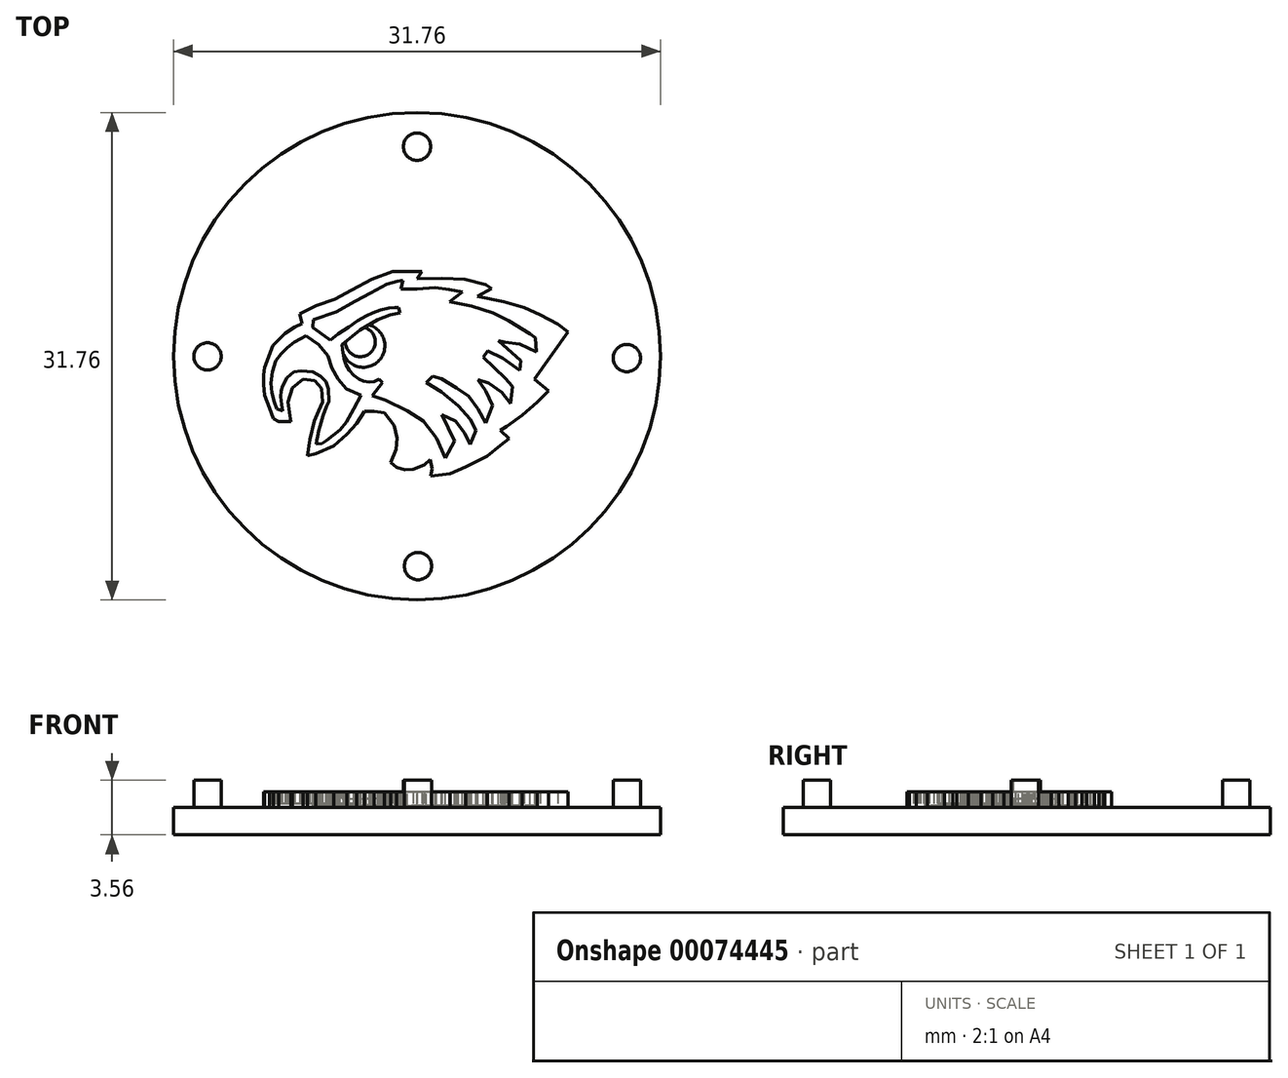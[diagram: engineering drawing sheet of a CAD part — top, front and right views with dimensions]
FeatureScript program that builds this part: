
annotation { "Feature Type Name" : "Feature", "Feature Type Description" : "" }
export const myFeature = defineFeature(function(context is Context, id is Id, definition is map)
    precondition{}
    {
        {
            var Q0;
            Q0=qCreatedBy(makeId("Top.planeOp"),FACE);
            var sketch = newSketch(context, id + "F0", { "sketchPlane" : qUnion([Q0])});
            skCircle(sketch, "E0", {"center": v(0, 0) * mm, "radius": 15.88 * mm});
            skSolve(sketch);
        }
        {
            var Q0;
            Q0=qSketchRegion(id+"F0",true);
            extrude(context, id + "F1", {"entities" : qUnion([Q0]), "oppositeDirection" : true, "depth" : 1.78 * mm});
        }
        {
            var Q0;
            Q0=makeQuery(id+"F1.opExtrude","CAP_FACE",FACE,{"disambiguationData":[OSD([sQuery(id+"F0.wireOp",EDGE,"E0")])],"isStart":true});
            var sketch = newSketch(context, id + "F2", { "sketchPlane" : qUnion([Q0])});
            skCircle(sketch, "E1", {"center": v(0, 0) * mm, "radius": 12.7 * mm});
            skSolve(sketch);
        }
        {
            var Q0;
            Q0=makeQuery(id+"F2.imprint","IMPRINT",FACE,{"disambiguationData":[TD([[makeQuery(id+"F2.imprint","IMPRINT",EDGE,{"derivedFrom":sQuery(id+"F2.wireOp",EDGE,"E1")}),-1.0]])]});
            var sketch = newSketch(context, id + "F3", { "sketchPlane" : qUnion([Q0])});
            skCircle(sketch, "E2", {"center": v(0, 13.65) * mm, "radius": 0.89 * mm});
            skCircle(sketch, "E3", {"center": v(-13.66, -0.02) * mm, "radius": 0.89 * mm});
            skCircle(sketch, "E4", {"center": v(0.06, -13.68) * mm, "radius": 0.89 * mm});
            skCircle(sketch, "E5", {"center": v(13.67, -0.12) * mm, "radius": 0.89 * mm});
            skSolve(sketch);
        }
        {
            var Q0;
            Q0=qSketchRegion(id+"F3",true);
            extrude(context, id + "F4", {"entities" : qUnion([Q0]), "operationType" : NewBodyOperationType.ADD, "depth" : 1.78 * mm});
        }
        {
            var Q0;
            Q0=makeQuery(id+"F2.imprint","IMPRINT",FACE,{"disambiguationData":[TD([[makeQuery(id+"F2.imprint","IMPRINT",EDGE,{"derivedFrom":sQuery(id+"F2.wireOp",EDGE,"E1")}),-1.0]])]});
            var sketch = newSketch(context, id + "F5", { "sketchPlane" : qUnion([Q0])});
            skLineSegment(sketch, "E6", {"start": v(-9.93, -2.55) * mm, "end": v(-10, -1.84) * mm});
            skLineSegment(sketch, "E7", {"start": v(-10, -1.22) * mm, "end": v(-9.93, -0.75) * mm});
            skLineSegment(sketch, "E8", {"start": v(-9.93, -0.75) * mm, "end": v(-9.42, 0.69) * mm});
            skLineSegment(sketch, "E9", {"start": v(-9.42, 0.69) * mm, "end": v(-8.6, 1.5) * mm});
            skLineSegment(sketch, "E10", {"start": v(-8.6, 1.5) * mm, "end": v(-7.97, 1.88) * mm});
            skLineSegment(sketch, "E11", {"start": v(-7.97, 1.88) * mm, "end": v(-7.5, 2.11) * mm});
            skLineSegment(sketch, "E12", {"start": v(-7.5, 2.11) * mm, "end": v(-7.66, 2.74) * mm});
            skLineSegment(sketch, "E13", {"start": v(-7.66, 2.74) * mm, "end": v(-6.58, 3.29) * mm});
            skLineSegment(sketch, "E14", {"start": v(-6.58, 3.29) * mm, "end": v(-5.36, 3.7) * mm});
            skLineSegment(sketch, "E15", {"start": v(-5.36, 3.7) * mm, "end": v(-4.25, 4.3) * mm});
            skLineSegment(sketch, "E16", {"start": v(-4.25, 4.3) * mm, "end": v(-2.97, 5.01) * mm});
            skLineSegment(sketch, "E17", {"start": v(-2.97, 5.01) * mm, "end": v(-1.58, 5.52) * mm});
            skLineSegment(sketch, "E18", {"start": v(-1.58, 5.52) * mm, "end": v(-1.4, 5.52) * mm});
            skLineSegment(sketch, "E19", {"start": v(-1.4, 5.52) * mm, "end": v(0, 5.52) * mm});
            skLineSegment(sketch, "E20", {"start": v(-0.55, 5.52) * mm, "end": v(0, 5.52) * mm});
            skLineSegment(sketch, "E21", {"start": v(-0.55, 5.52) * mm, "end": v(0.33, 5.52) * mm});
            skLineSegment(sketch, "E22", {"start": v(0.33, 5.52) * mm, "end": v(0, 5.04) * mm});
            skLineSegment(sketch, "E23", {"start": v(0, 5.04) * mm, "end": v(1.62, 5.08) * mm});
            skLineSegment(sketch, "E24", {"start": v(1.62, 5.08) * mm, "end": v(3.1, 5.01) * mm});
            skLineSegment(sketch, "E25", {"start": v(3.1, 5.01) * mm, "end": v(4.46, 4.67) * mm});
            skLineSegment(sketch, "E26", {"start": v(4.46, 4.67) * mm, "end": v(4.87, 4.4) * mm});
            skLineSegment(sketch, "E27", {"start": v(4.87, 4.4) * mm, "end": v(3.92, 3.9) * mm});
            skLineSegment(sketch, "E28", {"start": v(3.92, 3.9) * mm, "end": v(5.64, 3.56) * mm});
            skLineSegment(sketch, "E29", {"start": v(5.64, 3.56) * mm, "end": v(7, 3.15) * mm});
            skLineSegment(sketch, "E30", {"start": v(7, 3.15) * mm, "end": v(8.04, 2.68) * mm});
            skLineSegment(sketch, "E31", {"start": v(8.04, 2.68) * mm, "end": v(9.19, 2.07) * mm});
            skLineSegment(sketch, "E32", {"start": v(9.19, 2.07) * mm, "end": v(9.83, 1.57) * mm});
            skLineSegment(sketch, "E33", {"start": v(9.83, 1.57) * mm, "end": v(7.63, -1.5) * mm});
            skLineSegment(sketch, "E34", {"start": v(7.63, -1.5) * mm, "end": v(8.58, -2.25) * mm});
            skLineSegment(sketch, "E35", {"start": v(8.58, -2.25) * mm, "end": v(7.84, -3) * mm});
            skLineSegment(sketch, "E36", {"start": v(7.84, -3) * mm, "end": v(6.86, -3.83) * mm});
            skLineSegment(sketch, "E37", {"start": v(6.86, -3.83) * mm, "end": v(5.84, -4.58) * mm});
            skLineSegment(sketch, "E38", {"start": v(5.84, -4.58) * mm, "end": v(5.44, -4.85) * mm});
            skLineSegment(sketch, "E39", {"start": v(5.44, -4.85) * mm, "end": v(6.01, -5.39) * mm});
            skLineSegment(sketch, "E40", {"start": v(6.01, -5.39) * mm, "end": v(5.44, -5.83) * mm});
            skLineSegment(sketch, "E41", {"start": v(5.44, -5.83) * mm, "end": v(4.56, -6.5) * mm});
            skLineSegment(sketch, "E42", {"start": v(4.56, -6.5) * mm, "end": v(3.18, -7.21) * mm});
            skLineSegment(sketch, "E43", {"start": v(3.18, -7.21) * mm, "end": v(2.16, -7.65) * mm});
            skLineSegment(sketch, "E44", {"start": v(2.16, -7.65) * mm, "end": v(0.88, -7.82) * mm});
            skLineSegment(sketch, "E45", {"start": v(0.88, -7.82) * mm, "end": v(0.98, -7.35) * mm});
            skLineSegment(sketch, "E46", {"start": v(0.98, -7.35) * mm, "end": v(0.85, -6.74) * mm});
            skLineSegment(sketch, "E47", {"start": v(0.85, -6.74) * mm, "end": v(0.48, -7.08) * mm});
            skLineSegment(sketch, "E48", {"start": v(0.48, -7.08) * mm, "end": v(-0.27, -7.38) * mm});
            skLineSegment(sketch, "E49", {"start": v(-0.27, -7.38) * mm, "end": v(-0.8, -7.41) * mm});
            skLineSegment(sketch, "E50", {"start": v(-0.8, -7.41) * mm, "end": v(-1.35, -7.24) * mm});
            skLineSegment(sketch, "E51", {"start": v(-1.35, -7.24) * mm, "end": v(-1.72, -6.94) * mm});
            skLineSegment(sketch, "E52", {"start": v(-1.72, -6.94) * mm, "end": v(-1.38, -6.06) * mm});
            skLineSegment(sketch, "E53", {"start": v(-1.38, -6.06) * mm, "end": v(-1.31, -5.35) * mm});
            skLineSegment(sketch, "E54", {"start": v(-1.31, -5.35) * mm, "end": v(-1.48, -4.5) * mm});
            skLineSegment(sketch, "E55", {"start": v(-1.48, -4.5) * mm, "end": v(-2.12, -3.7) * mm});
            skLineSegment(sketch, "E56", {"start": v(-2.12, -3.7) * mm, "end": v(-2.8, -3.6) * mm});
            skLineSegment(sketch, "E57", {"start": v(-2.8, -3.6) * mm, "end": v(-3.44, -3.6) * mm});
            skLineSegment(sketch, "E58", {"start": v(-3.44, -3.6) * mm, "end": v(-3.95, -4.37) * mm});
            skLineSegment(sketch, "E59", {"start": v(-3.95, -4.37) * mm, "end": v(-4.59, -5.08) * mm});
            skLineSegment(sketch, "E60", {"start": v(-4.59, -5.08) * mm, "end": v(-5.43, -5.86) * mm});
            skLineSegment(sketch, "E61", {"start": v(-5.43, -5.86) * mm, "end": v(-6.61, -6.37) * mm});
            skLineSegment(sketch, "E62", {"start": v(-6.61, -6.37) * mm, "end": v(-7.15, -6.47) * mm});
            skLineSegment(sketch, "E63", {"start": v(-7.15, -6.47) * mm, "end": v(-6.99, -5.42) * mm});
            skLineSegment(sketch, "E64", {"start": v(-6.99, -5.42) * mm, "end": v(-6.72, -4.24) * mm});
            skLineSegment(sketch, "E65", {"start": v(-6.72, -4.24) * mm, "end": v(-6.41, -3.56) * mm});
            skLineSegment(sketch, "E66", {"start": v(-6.41, -3.56) * mm, "end": v(-6.18, -3) * mm});
            skLineSegment(sketch, "E67", {"start": v(-6.18, -3) * mm, "end": v(-6.2, -2.11) * mm});
            skLineSegment(sketch, "E68", {"start": v(-6.2, -2.11) * mm, "end": v(-6.68, -1.6) * mm});
            skLineSegment(sketch, "E69", {"start": v(-6.68, -1.6) * mm, "end": v(-7.42, -1.5) * mm});
            skLineSegment(sketch, "E70", {"start": v(-7.42, -1.5) * mm, "end": v(-8.13, -2.08) * mm});
            skLineSegment(sketch, "E71", {"start": v(-8.13, -2.08) * mm, "end": v(-8.4, -3) * mm});
            skLineSegment(sketch, "E72", {"start": v(-8.4, -3) * mm, "end": v(-8.3, -3.87) * mm});
            skLineSegment(sketch, "E73", {"start": v(-8.3, -3.87) * mm, "end": v(-8.24, -4.25) * mm});
            skLineSegment(sketch, "E74", {"start": v(-10, -1.22) * mm, "end": v(-10, -1.84) * mm});
            skLineSegment(sketch, "E75", {"start": v(-9.93, -2.55) * mm, "end": v(-9.63, -3.36) * mm});
            skLineSegment(sketch, "E76", {"start": v(-9.63, -3.36) * mm, "end": v(-9.36, -4.06) * mm});
            skLineSegment(sketch, "E77", {"start": v(-9.36, -4.06) * mm, "end": v(-9.02, -4.26) * mm});
            skLineSegment(sketch, "E78", {"start": v(-9.02, -4.26) * mm, "end": v(-8.24, -4.25) * mm});
            skSolve(sketch);
        }
        {
            var Q0;
            Q0=qSketchRegion(id+"F5",true);
            extrude(context, id + "F6", {"entities" : qUnion([Q0]), "operationType" : NewBodyOperationType.ADD, "depth" : 1.02 * mm});
        }
        {
            var Q0;
            Q0=makeQuery(id+"F6.opExtrude","CAP_FACE",FACE,{"disambiguationData":[OSD([sQuery(id+"F5.wireOp",EDGE,"0b11d9ce-b06c-452d-9449-327050158518"),sQuery(id+"F5.wireOp",EDGE,"0f71f0c5-6bf1-46cd-a3a2-b6e89a077792"),sQuery(id+"F5.wireOp",EDGE,"E6"),sQuery(id+"F5.wireOp",EDGE,"E7"),sQuery(id+"F5.wireOp",EDGE,"E8"),sQuery(id+"F5.wireOp",EDGE,"E9"),sQuery(id+"F5.wireOp",EDGE,"E10"),sQuery(id+"F5.wireOp",EDGE,"E11"),sQuery(id+"F5.wireOp",EDGE,"E12"),sQuery(id+"F5.wireOp",EDGE,"E13"),sQuery(id+"F5.wireOp",EDGE,"E14"),sQuery(id+"F5.wireOp",EDGE,"E15"),sQuery(id+"F5.wireOp",EDGE,"E16"),sQuery(id+"F5.wireOp",EDGE,"E17"),sQuery(id+"F5.wireOp",EDGE,"E18"),sQuery(id+"F5.wireOp",EDGE,"E19"),sQuery(id+"F5.wireOp",EDGE,"E21"),sQuery(id+"F5.wireOp",EDGE,"E22"),sQuery(id+"F5.wireOp",EDGE,"E23"),sQuery(id+"F5.wireOp",EDGE,"E24"),sQuery(id+"F5.wireOp",EDGE,"E25"),sQuery(id+"F5.wireOp",EDGE,"E26"),sQuery(id+"F5.wireOp",EDGE,"E27"),sQuery(id+"F5.wireOp",EDGE,"E28"),sQuery(id+"F5.wireOp",EDGE,"E29"),sQuery(id+"F5.wireOp",EDGE,"E30"),sQuery(id+"F5.wireOp",EDGE,"E31"),sQuery(id+"F5.wireOp",EDGE,"E32"),sQuery(id+"F5.wireOp",EDGE,"E33"),sQuery(id+"F5.wireOp",EDGE,"E34"),sQuery(id+"F5.wireOp",EDGE,"E35"),sQuery(id+"F5.wireOp",EDGE,"E36"),sQuery(id+"F5.wireOp",EDGE,"E37"),sQuery(id+"F5.wireOp",EDGE,"E38"),sQuery(id+"F5.wireOp",EDGE,"E39"),sQuery(id+"F5.wireOp",EDGE,"E40"),sQuery(id+"F5.wireOp",EDGE,"E41"),sQuery(id+"F5.wireOp",EDGE,"E42"),sQuery(id+"F5.wireOp",EDGE,"E43"),sQuery(id+"F5.wireOp",EDGE,"E44"),sQuery(id+"F5.wireOp",EDGE,"E45"),sQuery(id+"F5.wireOp",EDGE,"E46"),sQuery(id+"F5.wireOp",EDGE,"E47"),sQuery(id+"F5.wireOp",EDGE,"E48"),sQuery(id+"F5.wireOp",EDGE,"E49"),sQuery(id+"F5.wireOp",EDGE,"E50"),sQuery(id+"F5.wireOp",EDGE,"E51"),sQuery(id+"F5.wireOp",EDGE,"E52"),sQuery(id+"F5.wireOp",EDGE,"E53"),sQuery(id+"F5.wireOp",EDGE,"E54"),sQuery(id+"F5.wireOp",EDGE,"E55"),sQuery(id+"F5.wireOp",EDGE,"E56"),sQuery(id+"F5.wireOp",EDGE,"E57"),sQuery(id+"F5.wireOp",EDGE,"E58"),sQuery(id+"F5.wireOp",EDGE,"E59"),sQuery(id+"F5.wireOp",EDGE,"E60"),sQuery(id+"F5.wireOp",EDGE,"E61"),sQuery(id+"F5.wireOp",EDGE,"E62"),sQuery(id+"F5.wireOp",EDGE,"E63"),sQuery(id+"F5.wireOp",EDGE,"E64"),sQuery(id+"F5.wireOp",EDGE,"E65"),sQuery(id+"F5.wireOp",EDGE,"E66"),sQuery(id+"F5.wireOp",EDGE,"E67"),sQuery(id+"F5.wireOp",EDGE,"E68"),sQuery(id+"F5.wireOp",EDGE,"E69"),sQuery(id+"F5.wireOp",EDGE,"E70"),sQuery(id+"F5.wireOp",EDGE,"E71"),sQuery(id+"F5.wireOp",EDGE,"E72"),sQuery(id+"F5.wireOp",EDGE,"E73"),sQuery(id+"F5.wireOp",EDGE,"E74")])],"isStart":false});
            var sketch = newSketch(context, id + "F7", { "sketchPlane" : qUnion([Q0])});
            skLineSegment(sketch, "E79", {"start": v(6.7, -0.93) * mm, "end": v(5.58, -0.15) * mm});
            skLineSegment(sketch, "E80", {"start": v(5.58, -0.15) * mm, "end": v(4.6, 0.35) * mm});
            skLineSegment(sketch, "E81", {"start": v(4.6, 0.35) * mm, "end": v(4.3, -0.07) * mm});
            skLineSegment(sketch, "E82", {"start": v(4.3, -0.07) * mm, "end": v(5.75, -1.42) * mm});
            skLineSegment(sketch, "E83", {"start": v(4.47, -4.34) * mm, "end": v(3.98, -3.44) * mm});
            skLineSegment(sketch, "E84", {"start": v(3.98, -3.44) * mm, "end": v(3.36, -2.62) * mm});
            skLineSegment(sketch, "E85", {"start": v(3.36, -2.62) * mm, "end": v(2.58, -2.08) * mm});
            skLineSegment(sketch, "E86", {"start": v(2.58, -2.08) * mm, "end": v(1.6, -1.46) * mm});
            skLineSegment(sketch, "E87", {"start": v(1.6, -1.46) * mm, "end": v(1.02, -1.3) * mm});
            skLineSegment(sketch, "E88", {"start": v(1.02, -1.3) * mm, "end": v(0.6, -1.71) * mm});
            skLineSegment(sketch, "E89", {"start": v(0.6, -1.71) * mm, "end": v(1.6, -2.33) * mm});
            skLineSegment(sketch, "E90", {"start": v(1.6, -2.33) * mm, "end": v(2.7, -3.23) * mm});
            skLineSegment(sketch, "E91", {"start": v(2.7, -3.23) * mm, "end": v(3.44, -4.1) * mm});
            skLineSegment(sketch, "E92", {"start": v(1.84, -6.64) * mm, "end": v(1.26, -5.33) * mm});
            skLineSegment(sketch, "E93", {"start": v(1.26, -5.33) * mm, "end": v(0.4, -4.22) * mm});
            skLineSegment(sketch, "E94", {"start": v(0.4, -4.22) * mm, "end": v(-0.63, -3.56) * mm});
            skLineSegment(sketch, "E95", {"start": v(-0.63, -3.56) * mm, "end": v(-2.07, -2.86) * mm});
            skLineSegment(sketch, "E96", {"start": v(-2.07, -2.86) * mm, "end": v(-2.93, -2.57) * mm});
            skLineSegment(sketch, "E97", {"start": v(-2.93, -2.57) * mm, "end": v(-2.27, -1.71) * mm});
            skLineSegment(sketch, "E98", {"start": v(-2.27, -1.71) * mm, "end": v(-2.48, -1.5) * mm});
            skLineSegment(sketch, "E99", {"start": v(-3.71, 1.7) * mm, "end": v(-2.56, 2.36) * mm});
            skLineSegment(sketch, "E100", {"start": v(-2.56, 2.36) * mm, "end": v(-1.74, 2.69) * mm});
            skLineSegment(sketch, "E101", {"start": v(-1.74, 2.69) * mm, "end": v(-1.12, 2.81) * mm});
            skLineSegment(sketch, "E102", {"start": v(-6.75, 2.36) * mm, "end": v(-5.27, 2.9) * mm});
            skLineSegment(sketch, "E103", {"start": v(-5.27, 2.9) * mm, "end": v(-4.04, 3.6) * mm});
            skLineSegment(sketch, "E104", {"start": v(-4.04, 3.6) * mm, "end": v(-3.01, 4.13) * mm});
            skLineSegment(sketch, "E105", {"start": v(-3.01, 4.13) * mm, "end": v(-1.98, 4.7) * mm});
            skLineSegment(sketch, "E106", {"start": v(-1.98, 4.7) * mm, "end": v(-1.29, 4.87) * mm});
            skLineSegment(sketch, "E107", {"start": v(-1.29, 4.87) * mm, "end": v(-0.92, 4.95) * mm});
            skLineSegment(sketch, "E108", {"start": v(-0.92, 4.95) * mm, "end": v(-1.04, 4.38) * mm});
            skLineSegment(sketch, "E109", {"start": v(-1.04, 4.38) * mm, "end": v(-0.01, 4.38) * mm});
            skLineSegment(sketch, "E110", {"start": v(-0.01, 4.38) * mm, "end": v(1.18, 4.46) * mm});
            skLineSegment(sketch, "E111", {"start": v(1.18, 4.46) * mm, "end": v(2.09, 4.33) * mm});
            skLineSegment(sketch, "E112", {"start": v(2.09, 4.33) * mm, "end": v(2.95, 4.17) * mm});
            skLineSegment(sketch, "E113", {"start": v(2.95, 4.17) * mm, "end": v(2.13, 3.55) * mm});
            skLineSegment(sketch, "E114", {"start": v(2.13, 3.55) * mm, "end": v(3.57, 3.26) * mm});
            skLineSegment(sketch, "E115", {"start": v(3.57, 3.26) * mm, "end": v(4.97, 2.81) * mm});
            skLineSegment(sketch, "E116", {"start": v(4.97, 2.81) * mm, "end": v(5.95, 2.32) * mm});
            skLineSegment(sketch, "E117", {"start": v(5.95, 2.32) * mm, "end": v(7.35, 1.46) * mm});
            skLineSegment(sketch, "E118", {"start": v(-2.48, -1.5) * mm, "end": v(-2.78, -1.67) * mm});
            skLineSegment(sketch, "E119", {"start": v(-2.78, -1.67) * mm, "end": v(-3.13, -1.68) * mm});
            skLineSegment(sketch, "E120", {"start": v(-3.13, -1.68) * mm, "end": v(-3.5, -1.64) * mm});
            skLineSegment(sketch, "E121", {"start": v(-3.5, -1.64) * mm, "end": v(-3.8, -1.5) * mm});
            skLineSegment(sketch, "E122", {"start": v(-3.8, -1.5) * mm, "end": v(-4.13, -1.24) * mm});
            skLineSegment(sketch, "E123", {"start": v(-4.13, -1.24) * mm, "end": v(-4.4, -0.93) * mm});
            skLineSegment(sketch, "E124", {"start": v(-4.4, -0.93) * mm, "end": v(-4.63, -0.54) * mm});
            skLineSegment(sketch, "E125", {"start": v(-4.63, -0.54) * mm, "end": v(-4.78, -0.16) * mm});
            skLineSegment(sketch, "E126", {"start": v(-4.78, -0.16) * mm, "end": v(-4.85, 0.44) * mm});
            skLineSegment(sketch, "E127", {"start": v(-4.85, 0.44) * mm, "end": v(-4.9, 0.77) * mm});
            skLineSegment(sketch, "E128", {"start": v(-3.71, 1.7) * mm, "end": v(-4.9, 0.77) * mm});
            skLineSegment(sketch, "E129", {"start": v(7.76, 0.27) * mm, "end": v(6.69, 0.78) * mm});
            skLineSegment(sketch, "E130", {"start": v(6.69, 0.78) * mm, "end": v(5.72, 0.9) * mm});
            skLineSegment(sketch, "E131", {"start": v(5.72, 0.9) * mm, "end": v(5.3, 1) * mm});
            skLineSegment(sketch, "E132", {"start": v(5.3, 1) * mm, "end": v(6.77, -0.3) * mm});
            skLineSegment(sketch, "E133", {"start": v(6.77, -0.3) * mm, "end": v(6.7, -0.93) * mm});
            skLineSegment(sketch, "E134", {"start": v(7.35, 1.46) * mm, "end": v(7.72, 1.19) * mm});
            skLineSegment(sketch, "E135", {"start": v(7.72, 1.19) * mm, "end": v(7.76, 0.27) * mm});
            skLineSegment(sketch, "E136", {"start": v(5.75, -1.42) * mm, "end": v(6.21, -1.99) * mm});
            skLineSegment(sketch, "E137", {"start": v(6.21, -1.99) * mm, "end": v(6.1, -3.08) * mm});
            skLineSegment(sketch, "E138", {"start": v(6.1, -3.08) * mm, "end": v(5.5, -2.35) * mm});
            skLineSegment(sketch, "E139", {"start": v(5.5, -2.35) * mm, "end": v(4.68, -1.77) * mm});
            skLineSegment(sketch, "E140", {"start": v(4.68, -1.77) * mm, "end": v(3.98, -1.54) * mm});
            skLineSegment(sketch, "E141", {"start": v(3.98, -1.54) * mm, "end": v(4.47, -2.25) * mm});
            skLineSegment(sketch, "E142", {"start": v(4.47, -2.25) * mm, "end": v(4.91, -3.2) * mm});
            skLineSegment(sketch, "E143", {"start": v(4.91, -3.2) * mm, "end": v(4.47, -4.34) * mm});
            skLineSegment(sketch, "E144", {"start": v(3.44, -4.1) * mm, "end": v(3.82, -4.82) * mm});
            skLineSegment(sketch, "E145", {"start": v(3.82, -4.82) * mm, "end": v(3.47, -5.77) * mm});
            skLineSegment(sketch, "E146", {"start": v(3.47, -5.77) * mm, "end": v(3.1, -5.02) * mm});
            skLineSegment(sketch, "E147", {"start": v(3.1, -5.02) * mm, "end": v(2.5, -4.22) * mm});
            skLineSegment(sketch, "E148", {"start": v(2.5, -4.22) * mm, "end": v(1.62, -3.82) * mm});
            skLineSegment(sketch, "E149", {"start": v(1.62, -3.82) * mm, "end": v(2.46, -5.53) * mm});
            skLineSegment(sketch, "E150", {"start": v(2.46, -5.53) * mm, "end": v(1.84, -6.64) * mm});
            skLineSegment(sketch, "E151", {"start": v(-5.78, 1.12) * mm, "end": v(-6.8, 1.85) * mm});
            skLineSegment(sketch, "E152", {"start": v(-6.8, 1.85) * mm, "end": v(-6.75, 2.36) * mm});
            skLineSegment(sketch, "E153", {"start": v(-5.78, 1.12) * mm, "end": v(-5.66, 1.05) * mm});
            skLineSegment(sketch, "E154", {"start": v(-5.66, 1.05) * mm, "end": v(-5.15, 1.44) * mm});
            skLineSegment(sketch, "E155", {"start": v(-5.15, 1.44) * mm, "end": v(-4.44, 1.9) * mm});
            skLineSegment(sketch, "E156", {"start": v(-4.44, 1.9) * mm, "end": v(-3.86, 2.3) * mm});
            skLineSegment(sketch, "E157", {"start": v(-3.86, 2.3) * mm, "end": v(-3.31, 2.64) * mm});
            skLineSegment(sketch, "E158", {"start": v(-3.31, 2.64) * mm, "end": v(-2.9, 2.83) * mm});
            skLineSegment(sketch, "E159", {"start": v(-2.9, 2.83) * mm, "end": v(-2.38, 3.02) * mm});
            skLineSegment(sketch, "E160", {"start": v(-2.38, 3.02) * mm, "end": v(-1.83, 3.13) * mm});
            skLineSegment(sketch, "E161", {"start": v(-1.83, 3.13) * mm, "end": v(-1.45, 3.16) * mm});
            skLineSegment(sketch, "E162", {"start": v(-1.45, 3.16) * mm, "end": v(-1.2, 3.16) * mm});
            skLineSegment(sketch, "E163", {"start": v(-1.2, 3.16) * mm, "end": v(-1.12, 2.81) * mm});
            skSolve(sketch);
        }
        {
            var Q0;
            Q0=qSketchRegion(id+"F7",true);
            extrude(context, id + "F8", {"entities" : qUnion([Q0]), "operationType" : NewBodyOperationType.REMOVE, "oppositeDirection" : true, "depth" : 0.89 * mm});
        }
        {
            var Q0;
            Q0=makeQuery(id+"F6.opExtrude","CAP_FACE",FACE,{"disambiguationData":[OSD([sQuery(id+"F5.wireOp",EDGE,"0b11d9ce-b06c-452d-9449-327050158518"),sQuery(id+"F5.wireOp",EDGE,"0f71f0c5-6bf1-46cd-a3a2-b6e89a077792"),sQuery(id+"F5.wireOp",EDGE,"E6"),sQuery(id+"F5.wireOp",EDGE,"E7"),sQuery(id+"F5.wireOp",EDGE,"E8"),sQuery(id+"F5.wireOp",EDGE,"E9"),sQuery(id+"F5.wireOp",EDGE,"E10"),sQuery(id+"F5.wireOp",EDGE,"E11"),sQuery(id+"F5.wireOp",EDGE,"E12"),sQuery(id+"F5.wireOp",EDGE,"E13"),sQuery(id+"F5.wireOp",EDGE,"E14"),sQuery(id+"F5.wireOp",EDGE,"E15"),sQuery(id+"F5.wireOp",EDGE,"E16"),sQuery(id+"F5.wireOp",EDGE,"E17"),sQuery(id+"F5.wireOp",EDGE,"E18"),sQuery(id+"F5.wireOp",EDGE,"E19"),sQuery(id+"F5.wireOp",EDGE,"E21"),sQuery(id+"F5.wireOp",EDGE,"E22"),sQuery(id+"F5.wireOp",EDGE,"E23"),sQuery(id+"F5.wireOp",EDGE,"E24"),sQuery(id+"F5.wireOp",EDGE,"E25"),sQuery(id+"F5.wireOp",EDGE,"E26"),sQuery(id+"F5.wireOp",EDGE,"E27"),sQuery(id+"F5.wireOp",EDGE,"E28"),sQuery(id+"F5.wireOp",EDGE,"E29"),sQuery(id+"F5.wireOp",EDGE,"E30"),sQuery(id+"F5.wireOp",EDGE,"E31"),sQuery(id+"F5.wireOp",EDGE,"E32"),sQuery(id+"F5.wireOp",EDGE,"E33"),sQuery(id+"F5.wireOp",EDGE,"E34"),sQuery(id+"F5.wireOp",EDGE,"E35"),sQuery(id+"F5.wireOp",EDGE,"E36"),sQuery(id+"F5.wireOp",EDGE,"E37"),sQuery(id+"F5.wireOp",EDGE,"E38"),sQuery(id+"F5.wireOp",EDGE,"E39"),sQuery(id+"F5.wireOp",EDGE,"E40"),sQuery(id+"F5.wireOp",EDGE,"E41"),sQuery(id+"F5.wireOp",EDGE,"E42"),sQuery(id+"F5.wireOp",EDGE,"E43"),sQuery(id+"F5.wireOp",EDGE,"E44"),sQuery(id+"F5.wireOp",EDGE,"E45"),sQuery(id+"F5.wireOp",EDGE,"E46"),sQuery(id+"F5.wireOp",EDGE,"E47"),sQuery(id+"F5.wireOp",EDGE,"E48"),sQuery(id+"F5.wireOp",EDGE,"E49"),sQuery(id+"F5.wireOp",EDGE,"E50"),sQuery(id+"F5.wireOp",EDGE,"E51"),sQuery(id+"F5.wireOp",EDGE,"E52"),sQuery(id+"F5.wireOp",EDGE,"E53"),sQuery(id+"F5.wireOp",EDGE,"E54"),sQuery(id+"F5.wireOp",EDGE,"E55"),sQuery(id+"F5.wireOp",EDGE,"E56"),sQuery(id+"F5.wireOp",EDGE,"E57"),sQuery(id+"F5.wireOp",EDGE,"E58"),sQuery(id+"F5.wireOp",EDGE,"E59"),sQuery(id+"F5.wireOp",EDGE,"E60"),sQuery(id+"F5.wireOp",EDGE,"E61"),sQuery(id+"F5.wireOp",EDGE,"E62"),sQuery(id+"F5.wireOp",EDGE,"E63"),sQuery(id+"F5.wireOp",EDGE,"E64"),sQuery(id+"F5.wireOp",EDGE,"E65"),sQuery(id+"F5.wireOp",EDGE,"E66"),sQuery(id+"F5.wireOp",EDGE,"E67"),sQuery(id+"F5.wireOp",EDGE,"E68"),sQuery(id+"F5.wireOp",EDGE,"E69"),sQuery(id+"F5.wireOp",EDGE,"E70"),sQuery(id+"F5.wireOp",EDGE,"E71"),sQuery(id+"F5.wireOp",EDGE,"E72"),sQuery(id+"F5.wireOp",EDGE,"E73"),sQuery(id+"F5.wireOp",EDGE,"E74")])],"isStart":false});
            var sketch = newSketch(context, id + "F9", { "sketchPlane" : qUnion([Q0])});
            skLineSegment(sketch, "E164", {"start": v(-9.47, -2.38) * mm, "end": v(-9.53, -1.76) * mm});
            skLineSegment(sketch, "E165", {"start": v(-9.53, -1.76) * mm, "end": v(-9.43, -1.02) * mm});
            skLineSegment(sketch, "E166", {"start": v(-9.43, -1.02) * mm, "end": v(-9.2, -0.29) * mm});
            skLineSegment(sketch, "E167", {"start": v(-9.2, -0.29) * mm, "end": v(-8.85, 0.16) * mm});
            skLineSegment(sketch, "E168", {"start": v(-8.85, 0.16) * mm, "end": v(-8.46, 0.57) * mm});
            skLineSegment(sketch, "E169", {"start": v(-8.46, 0.57) * mm, "end": v(-8, 0.92) * mm});
            skLineSegment(sketch, "E170", {"start": v(-8, 0.92) * mm, "end": v(-7.6, 1.13) * mm});
            skLineSegment(sketch, "E171", {"start": v(-7.6, 1.13) * mm, "end": v(-7.26, 1.32) * mm});
            skLineSegment(sketch, "E172", {"start": v(-7.26, 1.32) * mm, "end": v(-6.43, 0.77) * mm});
            skLineSegment(sketch, "E173", {"start": v(-6.43, 0.77) * mm, "end": v(-5.8, 0.02) * mm});
            skLineSegment(sketch, "E174", {"start": v(-5.8, 0.02) * mm, "end": v(-5.57, -0.75) * mm});
            skLineSegment(sketch, "E175", {"start": v(-5.57, -0.75) * mm, "end": v(-5.16, -1.51) * mm});
            skLineSegment(sketch, "E176", {"start": v(-5.16, -1.51) * mm, "end": v(-4.62, -2.13) * mm});
            skLineSegment(sketch, "E177", {"start": v(-4.62, -2.13) * mm, "end": v(-3.67, -2.56) * mm});
            skLineSegment(sketch, "E178", {"start": v(-3.67, -2.56) * mm, "end": v(-4.13, -3.45) * mm});
            skLineSegment(sketch, "E179", {"start": v(-4.13, -3.45) * mm, "end": v(-4.62, -4.29) * mm});
            skLineSegment(sketch, "E180", {"start": v(-4.62, -4.29) * mm, "end": v(-5.02, -4.8) * mm});
            skLineSegment(sketch, "E181", {"start": v(-5.02, -4.8) * mm, "end": v(-5.9, -5.5) * mm});
            skLineSegment(sketch, "E182", {"start": v(-5.9, -5.5) * mm, "end": v(-6.2, -5.7) * mm});
            skLineSegment(sketch, "E183", {"start": v(-6.81, -1.02) * mm, "end": v(-7.55, -0.95) * mm});
            skLineSegment(sketch, "E184", {"start": v(-7.55, -0.95) * mm, "end": v(-8.03, -1.02) * mm});
            skLineSegment(sketch, "E185", {"start": v(-8.03, -1.02) * mm, "end": v(-8.48, -1.4) * mm});
            skLineSegment(sketch, "E186", {"start": v(-8.48, -1.4) * mm, "end": v(-8.75, -1.96) * mm});
            skLineSegment(sketch, "E187", {"start": v(-8.75, -1.96) * mm, "end": v(-8.85, -2.27) * mm});
            skLineSegment(sketch, "E188", {"start": v(-8.85, -2.27) * mm, "end": v(-8.89, -2.66) * mm});
            skLineSegment(sketch, "E189", {"start": v(-6.2, -5.7) * mm, "end": v(-6.59, -5.72) * mm});
            skLineSegment(sketch, "E190", {"start": v(-6.59, -5.72) * mm, "end": v(-6.54, -5.5) * mm});
            skLineSegment(sketch, "E191", {"start": v(-6.81, -1.02) * mm, "end": v(-6.29, -1.3) * mm});
            skLineSegment(sketch, "E192", {"start": v(-6.29, -1.3) * mm, "end": v(-5.93, -1.65) * mm});
            skLineSegment(sketch, "E193", {"start": v(-5.93, -1.65) * mm, "end": v(-5.78, -2.14) * mm});
            skLineSegment(sketch, "E194", {"start": v(-5.78, -2.14) * mm, "end": v(-5.76, -2.96) * mm});
            skLineSegment(sketch, "E195", {"start": v(-5.76, -2.96) * mm, "end": v(-5.9, -3.28) * mm});
            skLineSegment(sketch, "E196", {"start": v(-5.9, -3.28) * mm, "end": v(-6.13, -3.87) * mm});
            skLineSegment(sketch, "E197", {"start": v(-6.13, -3.87) * mm, "end": v(-6.33, -4.55) * mm});
            skLineSegment(sketch, "E198", {"start": v(-6.33, -4.55) * mm, "end": v(-6.41, -4.88) * mm});
            skLineSegment(sketch, "E199", {"start": v(-6.41, -4.88) * mm, "end": v(-6.48, -5.22) * mm});
            skLineSegment(sketch, "E200", {"start": v(-6.54, -5.5) * mm, "end": v(-6.48, -5.22) * mm});
            skLineSegment(sketch, "E201", {"start": v(-9.47, -2.38) * mm, "end": v(-9.32, -2.99) * mm});
            skLineSegment(sketch, "E202", {"start": v(-9.32, -2.99) * mm, "end": v(-9.16, -3.44) * mm});
            skLineSegment(sketch, "E203", {"start": v(-9.16, -3.44) * mm, "end": v(-8.76, -3.57) * mm});
            skLineSegment(sketch, "E204", {"start": v(-8.76, -3.57) * mm, "end": v(-8.84, -3.15) * mm});
            skLineSegment(sketch, "E205", {"start": v(-8.84, -3.15) * mm, "end": v(-8.89, -2.66) * mm});
            skSolve(sketch);
        }
        {
            var Q0;
            Q0=qSketchRegion(id+"F9",true);
            extrude(context, id + "F10", {"entities" : qUnion([Q0]), "operationType" : NewBodyOperationType.REMOVE, "oppositeDirection" : true, "depth" : 0.76 * mm});
        }
        {
            var Q0;
            Q0=makeQuery(id+"F8.boolean.opBoolean","COPY",FACE,{"derivedFrom":makeQuery(id+"F8.opExtrude","CAP_FACE",FACE,{"disambiguationData":[OSD([sQuery(id+"F7.wireOp",EDGE,"E79"),sQuery(id+"F7.wireOp",EDGE,"E80"),sQuery(id+"F7.wireOp",EDGE,"E81"),sQuery(id+"F7.wireOp",EDGE,"E82"),sQuery(id+"F7.wireOp",EDGE,"E83"),sQuery(id+"F7.wireOp",EDGE,"E84"),sQuery(id+"F7.wireOp",EDGE,"E85"),sQuery(id+"F7.wireOp",EDGE,"E86"),sQuery(id+"F7.wireOp",EDGE,"E87"),sQuery(id+"F7.wireOp",EDGE,"E88"),sQuery(id+"F7.wireOp",EDGE,"E89"),sQuery(id+"F7.wireOp",EDGE,"E90"),sQuery(id+"F7.wireOp",EDGE,"E91"),sQuery(id+"F7.wireOp",EDGE,"E92"),sQuery(id+"F7.wireOp",EDGE,"E93"),sQuery(id+"F7.wireOp",EDGE,"E94"),sQuery(id+"F7.wireOp",EDGE,"E95"),sQuery(id+"F7.wireOp",EDGE,"E96"),sQuery(id+"F7.wireOp",EDGE,"E97"),sQuery(id+"F7.wireOp",EDGE,"E98"),sQuery(id+"F7.wireOp",EDGE,"E99"),sQuery(id+"F7.wireOp",EDGE,"E100"),sQuery(id+"F7.wireOp",EDGE,"E101"),sQuery(id+"F7.wireOp",EDGE,"bZtnq0oz-B1nZ-lnwP-gbeB-6xsL7ujSwZ4H"),sQuery(id+"F7.wireOp",EDGE,"FM4iQwu3-wLjz-oE57-lWY5-Kczz2a4fD5oc"),sQuery(id+"F7.wireOp",EDGE,"3L7KJqvM-dJYk-JuSZ-hmax-Vh9DTnFLQWhU"),sQuery(id+"F7.wireOp",EDGE,"JWtqIWVs-Qr8e-em4D-xvaK-B1dK60s15yhR"),sQuery(id+"F7.wireOp",EDGE,"bkGlrWF0-D5oi-p2ix-DRx4-v5Btxe60QDYI"),sQuery(id+"F7.wireOp",EDGE,"omSeCV2j-FO6r-lofV-Fp1m-8OPX4g0BF3Ei"),sQuery(id+"F7.wireOp",EDGE,"4Bzy8rAQ-88cM-qlEE-GRoY-Cno2FRry2jiZ"),sQuery(id+"F7.wireOp",EDGE,"E102"),sQuery(id+"F7.wireOp",EDGE,"E103"),sQuery(id+"F7.wireOp",EDGE,"E104"),sQuery(id+"F7.wireOp",EDGE,"E105"),sQuery(id+"F7.wireOp",EDGE,"E106"),sQuery(id+"F7.wireOp",EDGE,"E107"),sQuery(id+"F7.wireOp",EDGE,"E108"),sQuery(id+"F7.wireOp",EDGE,"E109"),sQuery(id+"F7.wireOp",EDGE,"E110"),sQuery(id+"F7.wireOp",EDGE,"E111"),sQuery(id+"F7.wireOp",EDGE,"E112"),sQuery(id+"F7.wireOp",EDGE,"E113"),sQuery(id+"F7.wireOp",EDGE,"E114"),sQuery(id+"F7.wireOp",EDGE,"E115"),sQuery(id+"F7.wireOp",EDGE,"E116"),sQuery(id+"F7.wireOp",EDGE,"E117"),sQuery(id+"F7.wireOp",EDGE,"E118"),sQuery(id+"F7.wireOp",EDGE,"E119"),sQuery(id+"F7.wireOp",EDGE,"E120"),sQuery(id+"F7.wireOp",EDGE,"E121"),sQuery(id+"F7.wireOp",EDGE,"E122"),sQuery(id+"F7.wireOp",EDGE,"E123"),sQuery(id+"F7.wireOp",EDGE,"E124"),sQuery(id+"F7.wireOp",EDGE,"E125"),sQuery(id+"F7.wireOp",EDGE,"E126"),sQuery(id+"F7.wireOp",EDGE,"E127"),sQuery(id+"F7.wireOp",EDGE,"E128"),sQuery(id+"F7.wireOp",EDGE,"E129"),sQuery(id+"F7.wireOp",EDGE,"E130"),sQuery(id+"F7.wireOp",EDGE,"E131"),sQuery(id+"F7.wireOp",EDGE,"E132"),sQuery(id+"F7.wireOp",EDGE,"E133"),sQuery(id+"F7.wireOp",EDGE,"E134"),sQuery(id+"F7.wireOp",EDGE,"E135"),sQuery(id+"F7.wireOp",EDGE,"E136"),sQuery(id+"F7.wireOp",EDGE,"E137"),sQuery(id+"F7.wireOp",EDGE,"E138"),sQuery(id+"F7.wireOp",EDGE,"E139"),sQuery(id+"F7.wireOp",EDGE,"E140"),sQuery(id+"F7.wireOp",EDGE,"E141"),sQuery(id+"F7.wireOp",EDGE,"E142"),sQuery(id+"F7.wireOp",EDGE,"E143"),sQuery(id+"F7.wireOp",EDGE,"E144"),sQuery(id+"F7.wireOp",EDGE,"E145"),sQuery(id+"F7.wireOp",EDGE,"E146"),sQuery(id+"F7.wireOp",EDGE,"E147"),sQuery(id+"F7.wireOp",EDGE,"E148"),sQuery(id+"F7.wireOp",EDGE,"E149"),sQuery(id+"F7.wireOp",EDGE,"E150")])],"isStart":false})});
            var sketch = newSketch(context, id + "F11", { "sketchPlane" : qUnion([Q0])});
            skArc(sketch, "E206", {"start": v(-4.9, 0.77) * mm, "mid": v(-2.69, -0.47) * mm, "end": v(-3.14, 2.03) * mm});
            skLineSegment(sketch, "E207", {"start": v(-3.14, 2.03) * mm, "end": v(-3.71, 1.7) * mm});
            skLineSegment(sketch, "E208", {"start": v(-3.71, 1.7) * mm, "end": v(-4.9, 0.77) * mm});
            skSolve(sketch);
        }
        {
            var Q0;
            Q0 = qSketchRegion(id + "F11", true);
            extrude(context, id + "F12", {"entities" : qUnion([Q0]), "operationType" : NewBodyOperationType.ADD, "depth" : 0.45 * mm});
        }
        {
            var Q0;
            Q0=makeQuery(id+"F12.opExtrude","CAP_FACE",FACE,{"disambiguationData":[OSD([sQuery(id+"F11.wireOp",EDGE,"E206"),sQuery(id+"F11.wireOp",EDGE,"E207"),sQuery(id+"F11.wireOp",EDGE,"E208")])],"isStart":false});
            var sketch = newSketch(context, id + "F13", { "sketchPlane" : qUnion([Q0])});
            skArc(sketch, "E209", {"start": v(-4.67, 0.95) * mm, "mid": v(-3.12, 0.15) * mm, "end": v(-3.42, 1.87) * mm});
            skLineSegment(sketch, "E210", {"start": v(-3.42, 1.87) * mm, "end": v(-3.71, 1.7) * mm});
            skLineSegment(sketch, "E211", {"start": v(-3.71, 1.7) * mm, "end": v(-4.67, 0.95) * mm});
            skSolve(sketch);
        }
        {
            var Q0;
            Q0 = qSketchRegion(id + "F13", true);
            extrude(context, id + "F14", {"entities" : qUnion([Q0]), "operationType" : NewBodyOperationType.REMOVE, "oppositeDirection" : true, "depth" : 0.42 * mm});
        }
    });
